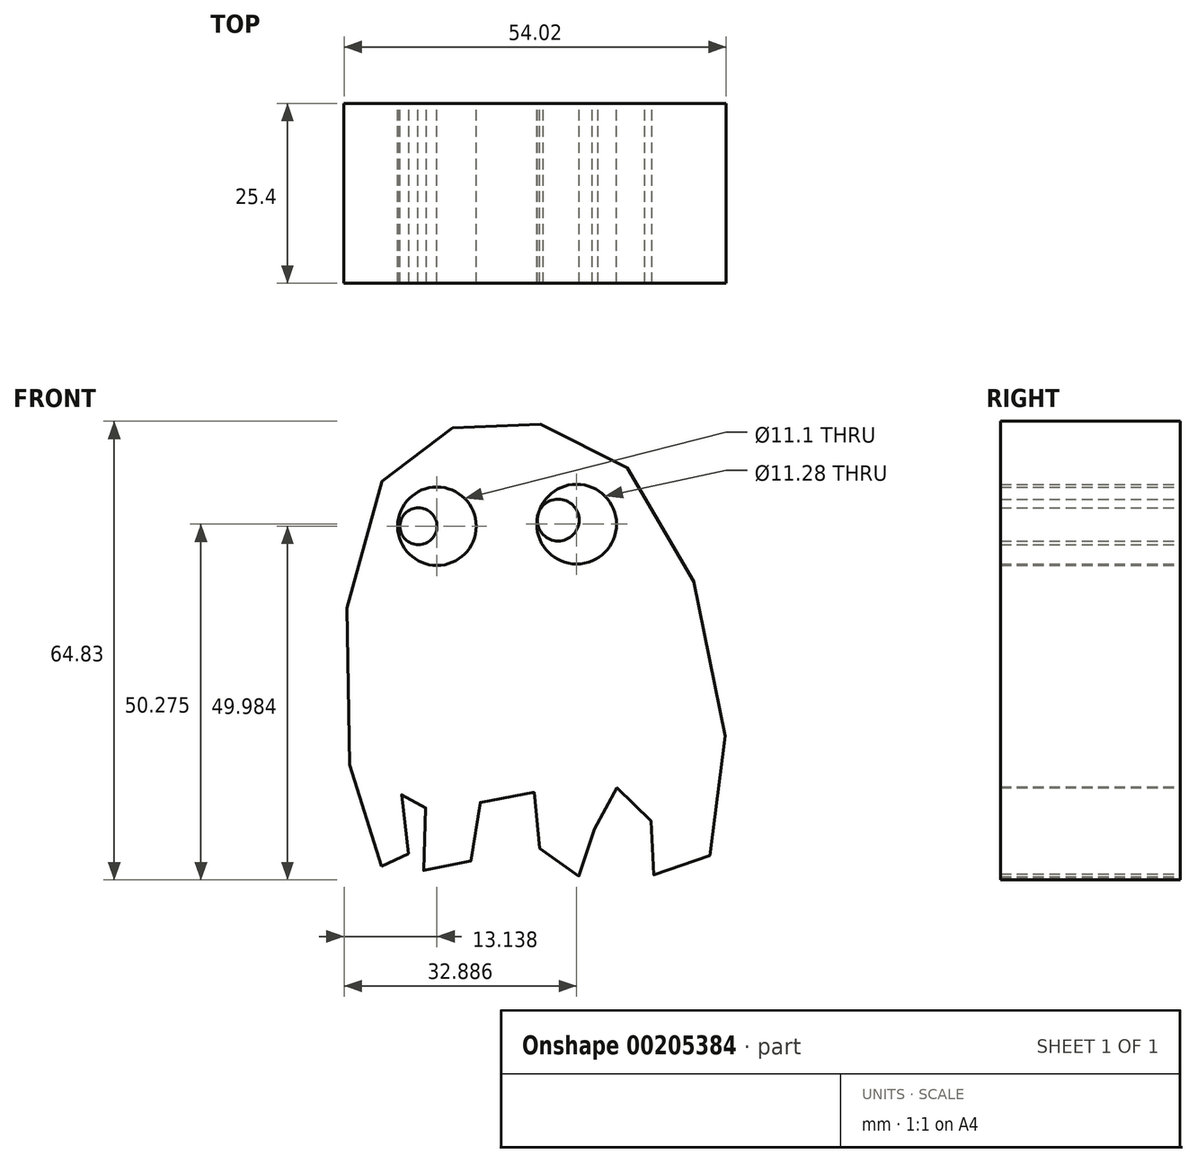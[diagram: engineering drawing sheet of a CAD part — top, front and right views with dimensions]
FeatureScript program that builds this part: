
annotation { "Feature Type Name" : "Feature", "Feature Type Description" : "" }
export const myFeature = defineFeature(function(context is Context, id is Id, definition is map)
    precondition{}
    {
        {
            var Q0;
            Q0=qCreatedBy(makeId("Front.planeOp"),FACE);
            var sketch = newSketch(context, id + "F0", { "sketchPlane" : qUnion([Q0])});
            skFitSpline(sketch, "E0", {"points": [v(-30.2, 0) * mm, v(-32.24, 50.1) * mm, v(-14.23, 62.88) * mm, v(9.3, 50.39) * mm, v(15.1, 0) * mm, v(7.26, 0) * mm, v(7.55, 9.44) * mm, v(0, 9.73) * mm, v(0, 0) * mm, v(-7.26, 0) * mm, v(-7.84, 9.73) * mm, v(-15.97, 9.44) * mm, v(-18, 0) * mm, v(-24.69, 0) * mm, v(-24.1, 10.6) * mm, v(-27.59, 9.73) * mm, v(-26.43, 0) * mm, v(-30.2, 0) * mm]});
            skCircle(sketch, "E1", {"center": v(-22.36, 48.06) * mm, "radius": 5.55 * mm});
            skCircle(sketch, "E2", {"center": v(-2.61, 48.35) * mm, "radius": 5.64 * mm});
            skCircle(sketch, "E3", {"center": v(-24.98, 48.06) * mm, "radius": 2.61 * mm});
            skCircle(sketch, "E4", {"center": v(-5.23, 48.94) * mm, "radius": 2.96 * mm});
            skSolve(sketch);
        }
        {
            var Q0;
            Q0=makeQuery(id+"F0.imprint","IMPRINT",FACE,{"disambiguationData":[TD([[makeQuery(id+"F0.imprint","IMPRINT",EDGE,{"derivedFrom":sQuery(id+"F0.wireOp",EDGE,"E0")}),-1.0]])]});
            var Q1;
            Q1=makeQuery(id+"F0.imprint","IMPRINT",FACE,{"disambiguationData":[TD([[makeQuery(id+"F0.imprint","IMPRINT",EDGE,{"derivedFrom":sQuery(id+"F0.wireOp",EDGE,"E3")}),1.0]])]});
            var Q2;
            Q2=makeQuery(id+"F0.imprint","IMPRINT",FACE,{"disambiguationData":[TD([[makeQuery(id+"F0.imprint","IMPRINT",EDGE,{"derivedFrom":sQuery(id+"F0.wireOp",EDGE,"E4")}),1.0]])]});
            extrude(context, id + "F1", {"entities" : qUnion([Q0, Q1, Q2]), "depth" : 25.4 * mm});
        }
    });
